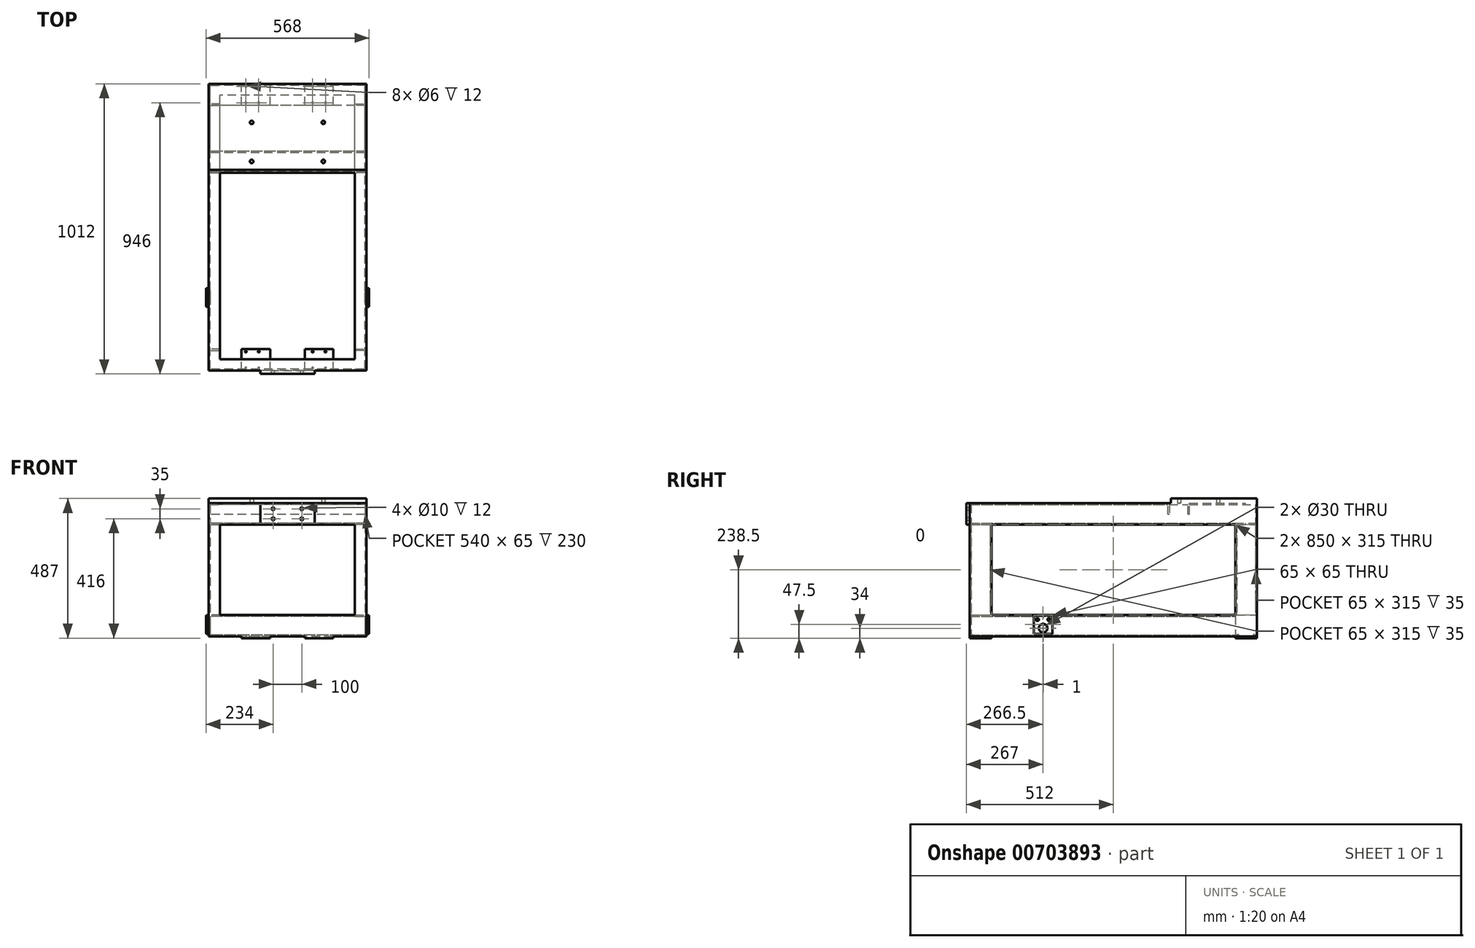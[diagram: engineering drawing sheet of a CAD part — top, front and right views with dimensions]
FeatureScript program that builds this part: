
annotation { "Feature Type Name" : "Feature", "Feature Type Description" : "" }
export const myFeature = defineFeature(function(context is Context, id is Id, definition is map)
    precondition{}
    {
        {
            var Q0;
            Q0=qCreatedBy(makeId("Front.planeOp"),FACE);
            var sketch = newSketch(context, id + "F0", { "sketchPlane" : qUnion([Q0])});
            skLineSegment(sketch, "E0", {"start": v(0, 32.91) * mm, "end": v(0, -75) * mm});
            skLineSegment(sketch, "E1", {"start": v(0, -75) * mm, "end": v(40, -75) * mm});
            skLineSegment(sketch, "E2", {"start": v(40, -75) * mm, "end": v(40, -70) * mm});
            skLineSegment(sketch, "E3", {"start": v(40, -70) * mm, "end": v(5, -70) * mm});
            skLineSegment(sketch, "E4", {"start": v(5, -70) * mm, "end": v(5, -5) * mm});
            skLineSegment(sketch, "E5", {"start": v(5, -5) * mm, "end": v(40, -5) * mm});
            skLineSegment(sketch, "E6", {"start": v(40, -5) * mm, "end": v(40, 0) * mm});
            skLineSegment(sketch, "E7", {"start": v(40, 0) * mm, "end": v(0, 0) * mm});
            skLineSegment(sketch, "E8.MirrorCS", {"start": v(510, -70) * mm, "end": v(545, -70) * mm});
            skLineSegment(sketch, "E9.MirrorCS", {"start": v(545, -70) * mm, "end": v(545, -5) * mm});
            skLineSegment(sketch, "E10.MirrorCS", {"start": v(545, -5) * mm, "end": v(510, -5) * mm});
            skLineSegment(sketch, "E11.MirrorCS", {"start": v(510, -5) * mm, "end": v(510, 0) * mm});
            skLineSegment(sketch, "E12.MirrorCS", {"start": v(510, 0) * mm, "end": v(550, 0) * mm});
            skLineSegment(sketch, "E13.MirrorCS", {"start": v(510, -75) * mm, "end": v(510, -70) * mm});
            skLineSegment(sketch, "E14.MirrorCS", {"start": v(550, 0) * mm, "end": v(550, -75) * mm});
            skLineSegment(sketch, "E15.MirrorCS", {"start": v(550, -75) * mm, "end": v(510, -75) * mm});
            skLineSegment(sketch, "E16", {"start": v(0, -357.09) * mm, "end": v(0, -465) * mm});
            skLineSegment(sketch, "E17", {"start": v(0, -465) * mm, "end": v(40, -465) * mm});
            skLineSegment(sketch, "E18", {"start": v(40, -465) * mm, "end": v(40, -460) * mm});
            skLineSegment(sketch, "E19", {"start": v(40, -460) * mm, "end": v(5, -460) * mm});
            skLineSegment(sketch, "E20", {"start": v(5, -460) * mm, "end": v(5, -395) * mm});
            skLineSegment(sketch, "E21", {"start": v(5, -395) * mm, "end": v(40, -395) * mm});
            skLineSegment(sketch, "E22", {"start": v(40, -395) * mm, "end": v(40, -390) * mm});
            skLineSegment(sketch, "E23", {"start": v(40, -390) * mm, "end": v(0, -390) * mm});
            skLineSegment(sketch, "E24.MirrorCS", {"start": v(510, -460) * mm, "end": v(545, -460) * mm});
            skLineSegment(sketch, "E25.MirrorCS", {"start": v(545, -460) * mm, "end": v(545, -395) * mm});
            skLineSegment(sketch, "E26.MirrorCS", {"start": v(545, -395) * mm, "end": v(510, -395) * mm});
            skLineSegment(sketch, "E27.MirrorCS", {"start": v(510, -395) * mm, "end": v(510, -390) * mm});
            skLineSegment(sketch, "E28.MirrorCS", {"start": v(510, -390) * mm, "end": v(550, -390) * mm});
            skLineSegment(sketch, "E29.MirrorCS", {"start": v(510, -465) * mm, "end": v(510, -460) * mm});
            skLineSegment(sketch, "E30.MirrorCS", {"start": v(550, -390) * mm, "end": v(550, -465) * mm});
            skLineSegment(sketch, "E31.MirrorCS", {"start": v(550, -465) * mm, "end": v(510, -465) * mm});
            skSolve(sketch);
        }
        {
            var Q0;
            {var subQ0=sQuery(id+"F0.wireOp",EDGE,"E1");Q0=makeQuery(id+"F0.imprint","IMPRINT",FACE,{"disambiguationData":[TD([[makeQuery(id+"F0.imprint","IMPRINT",EDGE,{"derivedFrom":subQ0}),1.0]])]});}
            var Q1;
            Q1=makeQuery(id+"F0.imprint","IMPRINT",FACE,{"disambiguationData":[TD([[makeQuery(id+"F0.imprint","IMPRINT",EDGE,{"derivedFrom":sQuery(id+"F0.wireOp",EDGE,"E8.MirrorCS")}),-1.0]])]});
            var Q2;
            {var subQ0=sQuery(id+"F0.wireOp",EDGE,"E17");Q2=makeQuery(id+"F0.imprint","IMPRINT",FACE,{"disambiguationData":[TD([[makeQuery(id+"F0.imprint","IMPRINT",EDGE,{"derivedFrom":subQ0}),1.0]])]});}
            var Q3;
            Q3=makeQuery(id+"F0.imprint","IMPRINT",FACE,{"disambiguationData":[TD([[makeQuery(id+"F0.imprint","IMPRINT",EDGE,{"derivedFrom":sQuery(id+"F0.wireOp",EDGE,"E24.MirrorCS")}),-1.0]])]});
            extrude(context, id + "F1", {"entities" : qUnion([Q0, Q1, Q2, Q3]), "depth" : 1000 * mm, "offsetDistance" : 25 * mm});
        }
        {
            var Q0;
            Q0=qCreatedBy(makeId("Right.planeOp"),FACE);
            var sketch = newSketch(context, id + "F2", { "sketchPlane" : qUnion([Q0])});
            skLineSegment(sketch, "E32", {"start": v(0, -75) * mm, "end": v(0, 0) * mm});
            skLineSegment(sketch, "E33", {"start": v(-40, 0) * mm, "end": v(-40, -5) * mm});
            skLineSegment(sketch, "E34", {"start": v(-40, -5) * mm, "end": v(-5, -5) * mm});
            skLineSegment(sketch, "E35", {"start": v(-5, -5) * mm, "end": v(-5, -70) * mm});
            skLineSegment(sketch, "E36", {"start": v(-5, -70) * mm, "end": v(-40, -70) * mm});
            skLineSegment(sketch, "E37", {"start": v(-40, -70) * mm, "end": v(-40, -75) * mm});
            skLineSegment(sketch, "E38", {"start": v(-40, -75) * mm, "end": v(0, -75) * mm});
            skLineSegment(sketch, "E39", {"start": v(-40, 0) * mm, "end": v(0, 0) * mm});
            skLineSegment(sketch, "E40.MirrorCS", {"start": v(-960, 0) * mm, "end": v(-960, -5) * mm});
            skLineSegment(sketch, "E41.MirrorCS", {"start": v(-960, -70) * mm, "end": v(-960, -75) * mm});
            skLineSegment(sketch, "E42.MirrorCS", {"start": v(-960, -5) * mm, "end": v(-995, -5) * mm});
            skLineSegment(sketch, "E43.MirrorCS", {"start": v(-995, -5) * mm, "end": v(-995, -70) * mm});
            skLineSegment(sketch, "E44.MirrorCS", {"start": v(-995, -70) * mm, "end": v(-960, -70) * mm});
            skLineSegment(sketch, "E45.MirrorCS", {"start": v(-960, 0) * mm, "end": v(-1000, 0) * mm});
            skLineSegment(sketch, "E46.MirrorCS", {"start": v(-1000, -75) * mm, "end": v(-1000, 0) * mm});
            skLineSegment(sketch, "E47.MirrorCS", {"start": v(-960, -75) * mm, "end": v(-1000, -75) * mm});
            skLineSegment(sketch, "E48.MirrorCS", {"start": v(-235, -40) * mm, "end": v(-240, -40) * mm});
            skLineSegment(sketch, "E49.MirrorCS", {"start": v(-305, -40) * mm, "end": v(-310, -40) * mm});
            skLineSegment(sketch, "E50.MirrorCS", {"start": v(-240, -40) * mm, "end": v(-240, -5) * mm});
            skLineSegment(sketch, "E51.MirrorCS", {"start": v(-240, -5) * mm, "end": v(-305, -5) * mm});
            skLineSegment(sketch, "E52.MirrorCS", {"start": v(-305, -5) * mm, "end": v(-305, -40) * mm});
            skLineSegment(sketch, "E53.MirrorCS", {"start": v(-235, -40) * mm, "end": v(-235, 0) * mm});
            skLineSegment(sketch, "E54.MirrorCS", {"start": v(-310, 0) * mm, "end": v(-235, 0) * mm});
            skLineSegment(sketch, "E55.MirrorCS", {"start": v(-310, -40) * mm, "end": v(-310, 0) * mm});
            skLineSegment(sketch, "E56.MirrorCS", {"start": v(-960, -390) * mm, "end": v(-960, -395) * mm});
            skLineSegment(sketch, "E57.MirrorCS", {"start": v(-960, -460) * mm, "end": v(-960, -465) * mm});
            skLineSegment(sketch, "E58.MirrorCS", {"start": v(-960, -395) * mm, "end": v(-995, -395) * mm});
            skLineSegment(sketch, "E59.MirrorCS", {"start": v(-995, -395) * mm, "end": v(-995, -460) * mm});
            skLineSegment(sketch, "E60.MirrorCS", {"start": v(-995, -460) * mm, "end": v(-960, -460) * mm});
            skLineSegment(sketch, "E61.MirrorCS", {"start": v(-960, -390) * mm, "end": v(-1000, -390) * mm});
            skLineSegment(sketch, "E62.MirrorCS", {"start": v(0, -465) * mm, "end": v(0, -390) * mm});
            skLineSegment(sketch, "E63.MirrorCS", {"start": v(-960, -465) * mm, "end": v(-1000, -465) * mm});
            skLineSegment(sketch, "E64", {"start": v(-1000, -465) * mm, "end": v(-1000, -390) * mm});
            skLineSegment(sketch, "E65.bottom", {"start": v(0, -390) * mm, "end": v(-75, -390) * mm});
            skLineSegment(sketch, "E65.top", {"start": v(0, -465) * mm, "end": v(-75, -465) * mm});
            skLineSegment(sketch, "E65.left", {"start": v(0, -390) * mm, "end": v(0, -465) * mm});
            skLineSegment(sketch, "E65.right", {"start": v(-75, -390) * mm, "end": v(-75, -465) * mm});
            skSolve(sketch);
        }
        {
            var Q0;
            Q0=qSketchRegion(id+"F2",true);
            extrude(context, id + "F3", {"entities" : qUnion([Q0]), "depth" : 550 * mm, "offsetDistance" : 25 * mm});
        }
        {
            var Q0;
            Q0=makeQuery(id+"F3.opExtrude","SWEPT_FACE",FACE,{"disambiguationData":[OSD([sQuery(id+"F2.wireOp",EDGE,"E65.bottom")])]});
            var sketch = newSketch(context, id + "F4", { "sketchPlane" : qUnion([Q0])});
            skLineSegment(sketch, "E66", {"start": v(0, -1000) * mm, "end": v(40, -1000) * mm});
            skLineSegment(sketch, "E67", {"start": v(40, -1000) * mm, "end": v(40, -995) * mm});
            skLineSegment(sketch, "E68", {"start": v(40, -995) * mm, "end": v(5, -995) * mm});
            skLineSegment(sketch, "E69", {"start": v(5, -995) * mm, "end": v(5, -930) * mm});
            skLineSegment(sketch, "E70", {"start": v(5, -930) * mm, "end": v(40, -930) * mm});
            skLineSegment(sketch, "E71", {"start": v(40, -930) * mm, "end": v(40, -925) * mm});
            skLineSegment(sketch, "E72", {"start": v(40, -925) * mm, "end": v(0, -925) * mm});
            skLineSegment(sketch, "E73.MirrorCS", {"start": v(510, -995) * mm, "end": v(545, -995) * mm});
            skLineSegment(sketch, "E74.MirrorCS", {"start": v(545, -995) * mm, "end": v(545, -930) * mm});
            skLineSegment(sketch, "E75.MirrorCS", {"start": v(545, -930) * mm, "end": v(510, -930) * mm});
            skLineSegment(sketch, "E76.MirrorCS", {"start": v(510, -930) * mm, "end": v(510, -925) * mm});
            skLineSegment(sketch, "E77.MirrorCS", {"start": v(510, -925) * mm, "end": v(550, -925) * mm});
            skLineSegment(sketch, "E78.MirrorCS", {"start": v(510, -1000) * mm, "end": v(510, -995) * mm});
            skLineSegment(sketch, "E79.MirrorCS", {"start": v(550, -925) * mm, "end": v(550, -1000) * mm});
            skLineSegment(sketch, "E80.MirrorCS", {"start": v(550, -1000) * mm, "end": v(510, -1000) * mm});
            skLineSegment(sketch, "E81", {"start": v(0, -1000) * mm, "end": v(0, -925) * mm});
            skLineSegment(sketch, "E82", {"start": v(0, -75) * mm, "end": v(40, -75) * mm});
            skLineSegment(sketch, "E83", {"start": v(40, -75) * mm, "end": v(40, -70) * mm});
            skLineSegment(sketch, "E84", {"start": v(40, -70) * mm, "end": v(5, -70) * mm});
            skLineSegment(sketch, "E85", {"start": v(5, -70) * mm, "end": v(5, -5) * mm});
            skLineSegment(sketch, "E86", {"start": v(5, -5) * mm, "end": v(40, -5) * mm});
            skLineSegment(sketch, "E87", {"start": v(40, -5) * mm, "end": v(40, 0) * mm});
            skLineSegment(sketch, "E88", {"start": v(40, 0) * mm, "end": v(0, 0) * mm});
            skLineSegment(sketch, "E89.MirrorCS", {"start": v(510, -70) * mm, "end": v(545, -70) * mm});
            skLineSegment(sketch, "E90.MirrorCS", {"start": v(545, -70) * mm, "end": v(545, -5) * mm});
            skLineSegment(sketch, "E91.MirrorCS", {"start": v(545, -5) * mm, "end": v(510, -5) * mm});
            skLineSegment(sketch, "E92.MirrorCS", {"start": v(510, -5) * mm, "end": v(510, 0) * mm});
            skLineSegment(sketch, "E93.MirrorCS", {"start": v(510, 0) * mm, "end": v(550, 0) * mm});
            skLineSegment(sketch, "E94.MirrorCS", {"start": v(510, -75) * mm, "end": v(510, -70) * mm});
            skLineSegment(sketch, "E95.MirrorCS", {"start": v(550, 0) * mm, "end": v(550, -75) * mm});
            skLineSegment(sketch, "E96.MirrorCS", {"start": v(550, -75) * mm, "end": v(510, -75) * mm});
            skLineSegment(sketch, "E97", {"start": v(0, -75) * mm, "end": v(0, 0) * mm});
            skSolve(sketch);
        }
        {
            var Q0;
            Q0 = qSketchRegion(id + "F4", true);
            extrude(context, id + "F5", {"entities" : qUnion([Q0]), "depth" : 315 * mm, "offsetDistance" : 25 * mm});
        }
        {
            var Q0;
            Q0=qCreatedBy(makeId("Top.planeOp"),FACE);
            var sketch = newSketch(context, id + "F6", { "sketchPlane" : qUnion([Q0])});
            skLineSegment(sketch, "E98.bottom", {"start": v(0, 0) * mm, "end": v(550, 0) * mm});
            skLineSegment(sketch, "E98.top", {"start": v(0, -300) * mm, "end": v(550, -300) * mm});
            skLineSegment(sketch, "E98.left", {"start": v(0, 0) * mm, "end": v(0, -300) * mm});
            skLineSegment(sketch, "E98.right", {"start": v(550, 0) * mm, "end": v(550, -300) * mm});
            skCircle(sketch, "E99", {"center": v(150, -134.83) * mm, "radius": 6 * mm});
            skCircle(sketch, "E100", {"center": v(400, -134.83) * mm, "radius": 6 * mm});
            skCircle(sketch, "E101", {"center": v(150, -270.83) * mm, "radius": 6 * mm});
            skCircle(sketch, "E102", {"center": v(400, -270.83) * mm, "radius": 6 * mm});
            skSolve(sketch);
        }
        {
            var Q0;
            Q0 = qSketchRegion(id + "F6", true);
            extrude(context, id + "F7", {"entities" : qUnion([Q0]), "depth" : 16 * mm, "offsetDistance" : 25 * mm});
        }
        {
            var Q0;
            Q0=makeQuery(id+"F3.opExtrude","SWEPT_FACE",FACE,{"disambiguationData":[OSD([sQuery(id+"F2.wireOp",EDGE,"E46.MirrorCS")])]});
            cPlane(context, id + "F8", {"entities" : qUnion([Q0]), "cplaneType" : CPlaneType.OFFSET, "offset" : 0 * mm, "width" : 150 * mm, "height" : 150 * mm});
        }
        {
            var Q0;
            Q0=qCreatedBy(id+"F8.planeOp",FACE);
            var sketch = newSketch(context, id + "F9", { "sketchPlane" : qUnion([Q0])});
            skLineSegment(sketch, "E103.bottom", {"start": v(370, 0) * mm, "end": v(180, 0) * mm});
            skLineSegment(sketch, "E103.top", {"start": v(370, -75) * mm, "end": v(180, -75) * mm});
            skLineSegment(sketch, "E103.left", {"start": v(370, 0) * mm, "end": v(370, -75) * mm});
            skLineSegment(sketch, "E103.right", {"start": v(180, 0) * mm, "end": v(180, -75) * mm});
            skCircle(sketch, "E104", {"center": v(225, -20) * mm, "radius": 5 * mm});
            skCircle(sketch, "E105", {"center": v(225, -55) * mm, "radius": 5 * mm});
            skCircle(sketch, "E106", {"center": v(325, -20) * mm, "radius": 5 * mm});
            skCircle(sketch, "E107", {"center": v(325, -55) * mm, "radius": 5 * mm});
            skSolve(sketch);
        }
        {
            var Q0;
            Q0 = qSketchRegion(id + "F9", true);
            extrude(context, id + "F10", {"entities" : qUnion([Q0]), "operationType" : NewBodyOperationType.ADD, "depth" : 12 * mm, "offsetDistance" : 25 * mm});
        }
        {
            var Q0;
            Q0=makeQuery(id+"F1.opExtrude","SWEPT_FACE",FACE,{"disambiguationData":[OSD([sQuery(id+"F0.wireOp",EDGE,"E31.MirrorCS")])]});
            cPlane(context, id + "F11", {"entities" : qUnion([Q0]), "cplaneType" : CPlaneType.OFFSET, "offset" : 0 * mm, "width" : 150 * mm, "height" : 150 * mm});
        }
        {
            var Q0;
            Q0=qCreatedBy(id+"F11.planeOp",FACE);
            var sketch = newSketch(context, id + "F12", { "sketchPlane" : qUnion([Q0])});
            skLineSegment(sketch, "E108.bottom", {"start": v(215, 75) * mm, "end": v(115, 75) * mm});
            skLineSegment(sketch, "E108.top", {"start": v(215, 0) * mm, "end": v(115, 0) * mm});
            skLineSegment(sketch, "E108.left", {"start": v(215, 75) * mm, "end": v(215, 0) * mm});
            skLineSegment(sketch, "E108.right", {"start": v(115, 75) * mm, "end": v(115, 0) * mm});
            skLineSegment(sketch, "E109.bottom", {"start": v(435, 75) * mm, "end": v(335, 75) * mm});
            skLineSegment(sketch, "E109.top", {"start": v(435, 0) * mm, "end": v(335, 0) * mm});
            skLineSegment(sketch, "E109.left", {"start": v(435, 75) * mm, "end": v(435, 0) * mm});
            skLineSegment(sketch, "E109.right", {"start": v(335, 75) * mm, "end": v(335, 0) * mm});
            skLineSegment(sketch, "E110.bottom", {"start": v(215, 1000) * mm, "end": v(115, 1000) * mm});
            skLineSegment(sketch, "E110.top", {"start": v(215, 925) * mm, "end": v(115, 925) * mm});
            skLineSegment(sketch, "E110.left", {"start": v(215, 1000) * mm, "end": v(215, 925) * mm});
            skLineSegment(sketch, "E110.right", {"start": v(115, 1000) * mm, "end": v(115, 925) * mm});
            skLineSegment(sketch, "E111.bottom", {"start": v(435, 1000) * mm, "end": v(335, 1000) * mm});
            skLineSegment(sketch, "E111.top", {"start": v(435, 925) * mm, "end": v(335, 925) * mm});
            skLineSegment(sketch, "E111.left", {"start": v(435, 1000) * mm, "end": v(435, 925) * mm});
            skLineSegment(sketch, "E111.right", {"start": v(335, 1000) * mm, "end": v(335, 925) * mm});
            skSolve(sketch);
        }
        {
            var Q0;
            Q0=makeQuery(id+"F1.opExtrude","SWEPT_BODY",BODY,{"disambiguationData":[OSD([sQuery(id+"F0.wireOp",EDGE,"E0"),sQuery(id+"F0.wireOp",EDGE,"E1"),sQuery(id+"F0.wireOp",EDGE,"E2"),sQuery(id+"F0.wireOp",EDGE,"E3"),sQuery(id+"F0.wireOp",EDGE,"E4"),sQuery(id+"F0.wireOp",EDGE,"E5"),sQuery(id+"F0.wireOp",EDGE,"E6"),sQuery(id+"F0.wireOp",EDGE,"E7")])]});
            var Q1;
            Q1=makeQuery(id+"F1.opExtrude","SWEPT_BODY",BODY,{"disambiguationData":[OSD([sQuery(id+"F0.wireOp",EDGE,"E8.MirrorCS"),sQuery(id+"F0.wireOp",EDGE,"E9.MirrorCS"),sQuery(id+"F0.wireOp",EDGE,"E10.MirrorCS"),sQuery(id+"F0.wireOp",EDGE,"E11.MirrorCS"),sQuery(id+"F0.wireOp",EDGE,"E12.MirrorCS"),sQuery(id+"F0.wireOp",EDGE,"E13.MirrorCS"),sQuery(id+"F0.wireOp",EDGE,"E14.MirrorCS"),sQuery(id+"F0.wireOp",EDGE,"E15.MirrorCS")])]});
            var Q2;
            Q2=makeQuery(id+"F1.opExtrude","SWEPT_BODY",BODY,{"disambiguationData":[OSD([sQuery(id+"F0.wireOp",EDGE,"E16"),sQuery(id+"F0.wireOp",EDGE,"E17"),sQuery(id+"F0.wireOp",EDGE,"E18"),sQuery(id+"F0.wireOp",EDGE,"E19"),sQuery(id+"F0.wireOp",EDGE,"E20"),sQuery(id+"F0.wireOp",EDGE,"E21"),sQuery(id+"F0.wireOp",EDGE,"E22"),sQuery(id+"F0.wireOp",EDGE,"E23")])]});
            var Q3;
            Q3=makeQuery(id+"F1.opExtrude","SWEPT_BODY",BODY,{"disambiguationData":[OSD([sQuery(id+"F0.wireOp",EDGE,"E24.MirrorCS"),sQuery(id+"F0.wireOp",EDGE,"E25.MirrorCS"),sQuery(id+"F0.wireOp",EDGE,"E26.MirrorCS"),sQuery(id+"F0.wireOp",EDGE,"E27.MirrorCS"),sQuery(id+"F0.wireOp",EDGE,"E28.MirrorCS"),sQuery(id+"F0.wireOp",EDGE,"E29.MirrorCS"),sQuery(id+"F0.wireOp",EDGE,"E30.MirrorCS"),sQuery(id+"F0.wireOp",EDGE,"E31.MirrorCS")])]});
            var Q4;
            Q4=makeQuery(id+"F3.opExtrude","SWEPT_BODY",BODY,{"disambiguationData":[OSD([sQuery(id+"F2.wireOp",EDGE,"E32"),sQuery(id+"F2.wireOp",EDGE,"E33"),sQuery(id+"F2.wireOp",EDGE,"E34"),sQuery(id+"F2.wireOp",EDGE,"E35"),sQuery(id+"F2.wireOp",EDGE,"E36"),sQuery(id+"F2.wireOp",EDGE,"E37"),sQuery(id+"F2.wireOp",EDGE,"E38"),sQuery(id+"F2.wireOp",EDGE,"E39")])]});
            var Q5;
            Q5=makeQuery(id+"F3.opExtrude","SWEPT_BODY",BODY,{"disambiguationData":[OSD([sQuery(id+"F2.wireOp",EDGE,"E56.MirrorCS"),sQuery(id+"F2.wireOp",EDGE,"E57.MirrorCS"),sQuery(id+"F2.wireOp",EDGE,"E58.MirrorCS"),sQuery(id+"F2.wireOp",EDGE,"E59.MirrorCS"),sQuery(id+"F2.wireOp",EDGE,"E60.MirrorCS"),sQuery(id+"F2.wireOp",EDGE,"E61.MirrorCS"),sQuery(id+"F2.wireOp",EDGE,"E63.MirrorCS"),sQuery(id+"F2.wireOp",EDGE,"E64")])]});
            var Q6;
            Q6=makeQuery(id+"F5.opExtrude","SWEPT_BODY",BODY,{"disambiguationData":[OSD([sQuery(id+"F4.wireOp",EDGE,"E73.MirrorCS"),sQuery(id+"F4.wireOp",EDGE,"E74.MirrorCS"),sQuery(id+"F4.wireOp",EDGE,"E75.MirrorCS"),sQuery(id+"F4.wireOp",EDGE,"E76.MirrorCS"),sQuery(id+"F4.wireOp",EDGE,"E77.MirrorCS"),sQuery(id+"F4.wireOp",EDGE,"E78.MirrorCS"),sQuery(id+"F4.wireOp",EDGE,"E79.MirrorCS"),sQuery(id+"F4.wireOp",EDGE,"E80.MirrorCS")])]});
            var Q7;
            Q7=makeQuery(id+"F7.opExtrude","SWEPT_BODY",BODY,{"disambiguationData":[OSD([sQuery(id+"F6.wireOp",EDGE,"E98.bottom"),sQuery(id+"F6.wireOp",EDGE,"E98.top"),sQuery(id+"F6.wireOp",EDGE,"E98.left"),sQuery(id+"F6.wireOp",EDGE,"E98.right"),sQuery(id+"F6.wireOp",EDGE,"E99"),sQuery(id+"F6.wireOp",EDGE,"E100"),sQuery(id+"F6.wireOp",EDGE,"E101"),sQuery(id+"F6.wireOp",EDGE,"E102")])]});
            var Q8;
            Q8=makeQuery(id+"F3.opExtrude","SWEPT_BODY",BODY,{"disambiguationData":[OSD([sQuery(id+"F2.wireOp",EDGE,"E40.MirrorCS"),sQuery(id+"F2.wireOp",EDGE,"E41.MirrorCS"),sQuery(id+"F2.wireOp",EDGE,"E42.MirrorCS"),sQuery(id+"F2.wireOp",EDGE,"E43.MirrorCS"),sQuery(id+"F2.wireOp",EDGE,"E44.MirrorCS"),sQuery(id+"F2.wireOp",EDGE,"E45.MirrorCS"),sQuery(id+"F2.wireOp",EDGE,"E46.MirrorCS"),sQuery(id+"F2.wireOp",EDGE,"E47.MirrorCS")])]});
            var Q9;
            Q9=makeQuery(id+"F3.opExtrude","SWEPT_BODY",BODY,{"disambiguationData":[OSD([sQuery(id+"F2.wireOp",EDGE,"E48.MirrorCS"),sQuery(id+"F2.wireOp",EDGE,"E49.MirrorCS"),sQuery(id+"F2.wireOp",EDGE,"E50.MirrorCS"),sQuery(id+"F2.wireOp",EDGE,"E51.MirrorCS"),sQuery(id+"F2.wireOp",EDGE,"E52.MirrorCS"),sQuery(id+"F2.wireOp",EDGE,"E53.MirrorCS"),sQuery(id+"F2.wireOp",EDGE,"E54.MirrorCS"),sQuery(id+"F2.wireOp",EDGE,"E55.MirrorCS")])]});
            var Q10;
            Q10=makeQuery(id+"F3.opExtrude","SWEPT_BODY",BODY,{"disambiguationData":[OSD([sQuery(id+"F2.wireOp",EDGE,"E65.bottom"),sQuery(id+"F2.wireOp",EDGE,"E65.top"),sQuery(id+"F2.wireOp",EDGE,"E65.left"),sQuery(id+"F2.wireOp",EDGE,"E65.right")])]});
            var Q11;
            Q11=makeQuery(id+"F5.opExtrude","SWEPT_BODY",BODY,{"disambiguationData":[OSD([sQuery(id+"F4.wireOp",EDGE,"E66"),sQuery(id+"F4.wireOp",EDGE,"E67"),sQuery(id+"F4.wireOp",EDGE,"E68"),sQuery(id+"F4.wireOp",EDGE,"E69"),sQuery(id+"F4.wireOp",EDGE,"E70"),sQuery(id+"F4.wireOp",EDGE,"E71"),sQuery(id+"F4.wireOp",EDGE,"E72"),sQuery(id+"F4.wireOp",EDGE,"E81")])]});
            var Q12;
            Q12=makeQuery(id+"F5.opExtrude","SWEPT_BODY",BODY,{"disambiguationData":[OSD([sQuery(id+"F4.wireOp",EDGE,"E82"),sQuery(id+"F4.wireOp",EDGE,"E83"),sQuery(id+"F4.wireOp",EDGE,"E84"),sQuery(id+"F4.wireOp",EDGE,"E85"),sQuery(id+"F4.wireOp",EDGE,"E86"),sQuery(id+"F4.wireOp",EDGE,"E87"),sQuery(id+"F4.wireOp",EDGE,"E88"),sQuery(id+"F4.wireOp",EDGE,"E97")])]});
            var Q13;
            Q13=makeQuery(id+"F5.opExtrude","SWEPT_BODY",BODY,{"disambiguationData":[OSD([sQuery(id+"F4.wireOp",EDGE,"E89.MirrorCS"),sQuery(id+"F4.wireOp",EDGE,"E90.MirrorCS"),sQuery(id+"F4.wireOp",EDGE,"E91.MirrorCS"),sQuery(id+"F4.wireOp",EDGE,"E92.MirrorCS"),sQuery(id+"F4.wireOp",EDGE,"E93.MirrorCS"),sQuery(id+"F4.wireOp",EDGE,"E94.MirrorCS"),sQuery(id+"F4.wireOp",EDGE,"E95.MirrorCS"),sQuery(id+"F4.wireOp",EDGE,"E96.MirrorCS")])]});
            booleanBodies(context, id + "F13", {"operationType" : BooleanOperationType.UNION, "tools" : qUnion([Q0, Q1, Q2, Q3, Q4, Q5, Q6, Q7, Q8, Q9, Q10, Q11, Q12, Q13])});
        }
        {
            var Q0;
            Q0 = qSketchRegion(id + "F12", true);
            extrude(context, id + "F14", {"entities" : qUnion([Q0]), "operationType" : NewBodyOperationType.ADD, "depth" : 6 * mm, "offsetDistance" : 25 * mm});
        }
        {
            var Q0;
            Q0=makeQuery(id+"F14.opExtrude","CAP_FACE",FACE,{"disambiguationData":[OSD([sQuery(id+"F12.wireOp",EDGE,"E111.bottom"),sQuery(id+"F12.wireOp",EDGE,"E111.top"),sQuery(id+"F12.wireOp",EDGE,"E111.left"),sQuery(id+"F12.wireOp",EDGE,"E111.right")])],"isStart":false});
            cPlane(context, id + "F15", {"entities" : qUnion([Q0]), "cplaneType" : CPlaneType.OFFSET, "offset" : 0 * mm, "width" : 150 * mm, "height" : 150 * mm});
        }
        {
            var Q0;
            Q0=qCreatedBy(id+"F15.planeOp",FACE);
            var sketch = newSketch(context, id + "F16", { "sketchPlane" : qUnion([Q0])});
            skCircle(sketch, "E112", {"center": v(407.5, 934) * mm, "radius": 3 * mm});
            skCircle(sketch, "E113", {"center": v(407.5, 991) * mm, "radius": 3 * mm});
            skCircle(sketch, "E114", {"center": v(362.5, 991) * mm, "radius": 3 * mm});
            skCircle(sketch, "E115", {"center": v(362.5, 934) * mm, "radius": 3 * mm});
            skCircle(sketch, "E116", {"center": v(407.5, 9) * mm, "radius": 3 * mm});
            skCircle(sketch, "E117", {"center": v(407.5, 66) * mm, "radius": 3 * mm});
            skCircle(sketch, "E118", {"center": v(362.5, 66) * mm, "radius": 3 * mm});
            skCircle(sketch, "E119", {"center": v(362.5, 9) * mm, "radius": 3 * mm});
            skCircle(sketch, "E120", {"center": v(174.84, 934) * mm, "radius": 3 * mm});
            skCircle(sketch, "E121", {"center": v(174.84, 991) * mm, "radius": 3 * mm});
            skCircle(sketch, "E122", {"center": v(129.84, 991) * mm, "radius": 3 * mm});
            skCircle(sketch, "E123", {"center": v(129.84, 934) * mm, "radius": 3 * mm});
            skCircle(sketch, "E124", {"center": v(174.84, 9) * mm, "radius": 3 * mm});
            skCircle(sketch, "E125", {"center": v(174.84, 66) * mm, "radius": 3 * mm});
            skCircle(sketch, "E126", {"center": v(129.84, 66) * mm, "radius": 3 * mm});
            skCircle(sketch, "E127", {"center": v(129.84, 9) * mm, "radius": 3 * mm});
            skSolve(sketch);
        }
        {
            var Q0;
            Q0 = qSketchRegion(id + "F16", true);
            extrude(context, id + "F17", {"entities" : qUnion([Q0]), "operationType" : NewBodyOperationType.REMOVE, "oppositeDirection" : true, "depth" : 12 * mm, "offsetDistance" : 25 * mm});
        }
        {
            var Q0;
            Q0=qCreatedBy(makeId("Right.planeOp"),FACE);
            var sketch = newSketch(context, id + "F18", { "sketchPlane" : qUnion([Q0])});
            skLineSegment(sketch, "E128.bottom", {"start": v(-712.5, -391) * mm, "end": v(-777.5, -391) * mm});
            skLineSegment(sketch, "E128.top", {"start": v(-712.5, -456) * mm, "end": v(-777.5, -456) * mm});
            skLineSegment(sketch, "E128.left", {"start": v(-712.5, -391) * mm, "end": v(-712.5, -456) * mm});
            skLineSegment(sketch, "E128.right", {"start": v(-777.5, -391) * mm, "end": v(-777.5, -456) * mm});
            skSolve(sketch);
        }
        {
            var Q0;
            Q0 = qSketchRegion(id + "F18", true);
            extrude(context, id + "F19", {"entities" : qUnion([Q0]), "operationType" : NewBodyOperationType.ADD, "oppositeDirection" : true, "depth" : 9 * mm, "offsetDistance" : 25 * mm});
        }
        {
            var Q0;
            Q0=makeQuery(id+"F13.opBoolean","MERGE",FACE,{"derivedFrom":[makeQuery(id+"F1.opExtrude","SWEPT_FACE",FACE,{"disambiguationData":[OSD([sQuery(id+"F0.wireOp",EDGE,"E14.MirrorCS")])]}),makeQuery(id+"F1.opExtrude","SWEPT_FACE",FACE,{"disambiguationData":[OSD([sQuery(id+"F0.wireOp",EDGE,"E30.MirrorCS")])]}),makeQuery(id+"F3.opExtrude","CAP_FACE",FACE,{"disambiguationData":[OSD([sQuery(id+"F2.wireOp",EDGE,"E32"),sQuery(id+"F2.wireOp",EDGE,"E33"),sQuery(id+"F2.wireOp",EDGE,"E34"),sQuery(id+"F2.wireOp",EDGE,"E35"),sQuery(id+"F2.wireOp",EDGE,"E36"),sQuery(id+"F2.wireOp",EDGE,"E37"),sQuery(id+"F2.wireOp",EDGE,"E38"),sQuery(id+"F2.wireOp",EDGE,"E39")])],"isStart":false}),makeQuery(id+"F3.opExtrude","CAP_FACE",FACE,{"disambiguationData":[OSD([sQuery(id+"F2.wireOp",EDGE,"E40.MirrorCS"),sQuery(id+"F2.wireOp",EDGE,"E41.MirrorCS"),sQuery(id+"F2.wireOp",EDGE,"E42.MirrorCS"),sQuery(id+"F2.wireOp",EDGE,"E43.MirrorCS"),sQuery(id+"F2.wireOp",EDGE,"E44.MirrorCS"),sQuery(id+"F2.wireOp",EDGE,"E45.MirrorCS"),sQuery(id+"F2.wireOp",EDGE,"E46.MirrorCS"),sQuery(id+"F2.wireOp",EDGE,"E47.MirrorCS")])],"isStart":false}),makeQuery(id+"F3.opExtrude","CAP_FACE",FACE,{"disambiguationData":[OSD([sQuery(id+"F2.wireOp",EDGE,"E48.MirrorCS"),sQuery(id+"F2.wireOp",EDGE,"E49.MirrorCS"),sQuery(id+"F2.wireOp",EDGE,"E50.MirrorCS"),sQuery(id+"F2.wireOp",EDGE,"E51.MirrorCS"),sQuery(id+"F2.wireOp",EDGE,"E52.MirrorCS"),sQuery(id+"F2.wireOp",EDGE,"E53.MirrorCS"),sQuery(id+"F2.wireOp",EDGE,"E54.MirrorCS"),sQuery(id+"F2.wireOp",EDGE,"E55.MirrorCS")])],"isStart":false}),makeQuery(id+"F3.opExtrude","CAP_FACE",FACE,{"disambiguationData":[OSD([sQuery(id+"F2.wireOp",EDGE,"E56.MirrorCS"),sQuery(id+"F2.wireOp",EDGE,"E57.MirrorCS"),sQuery(id+"F2.wireOp",EDGE,"E58.MirrorCS"),sQuery(id+"F2.wireOp",EDGE,"E59.MirrorCS"),sQuery(id+"F2.wireOp",EDGE,"E60.MirrorCS"),sQuery(id+"F2.wireOp",EDGE,"E61.MirrorCS"),sQuery(id+"F2.wireOp",EDGE,"E63.MirrorCS"),sQuery(id+"F2.wireOp",EDGE,"E64")])],"isStart":false}),makeQuery(id+"F3.opExtrude","CAP_FACE",FACE,{"disambiguationData":[OSD([sQuery(id+"F2.wireOp",EDGE,"E65.bottom"),sQuery(id+"F2.wireOp",EDGE,"E65.top"),sQuery(id+"F2.wireOp",EDGE,"E65.left"),sQuery(id+"F2.wireOp",EDGE,"E65.right")])],"isStart":false}),makeQuery(id+"F5.opExtrude","SWEPT_FACE",FACE,{"disambiguationData":[OSD([sQuery(id+"F4.wireOp",EDGE,"E79.MirrorCS")])]}),makeQuery(id+"F5.opExtrude","SWEPT_FACE",FACE,{"disambiguationData":[OSD([sQuery(id+"F4.wireOp",EDGE,"E95.MirrorCS")])]}),makeQuery(id+"F7.opExtrude","SWEPT_FACE",FACE,{"disambiguationData":[OSD([sQuery(id+"F6.wireOp",EDGE,"E98.right")])]})]});
            cPlane(context, id + "F20", {"entities" : qUnion([Q0]), "cplaneType" : CPlaneType.OFFSET, "offset" : 0 * mm, "width" : 150 * mm, "height" : 150 * mm});
        }
        {
            var Q0;
            Q0=qCreatedBy(id+"F20.planeOp",FACE);
            var sketch = newSketch(context, id + "F21", { "sketchPlane" : qUnion([Q0])});
            skLineSegment(sketch, "E129.bottom", {"start": v(-712.5, -391) * mm, "end": v(-777.5, -391) * mm});
            skLineSegment(sketch, "E129.top", {"start": v(-712.5, -456) * mm, "end": v(-777.5, -456) * mm});
            skLineSegment(sketch, "E129.left", {"start": v(-712.5, -391) * mm, "end": v(-712.5, -456) * mm});
            skLineSegment(sketch, "E129.right", {"start": v(-777.5, -391) * mm, "end": v(-777.5, -456) * mm});
            skSolve(sketch);
        }
        {
            var Q0;
            Q0 = qSketchRegion(id + "F21", true);
            extrude(context, id + "F22", {"entities" : qUnion([Q0]), "operationType" : NewBodyOperationType.ADD, "depth" : 9 * mm, "offsetDistance" : 25 * mm});
        }
        {
            var Q0;
            Q0=makeQuery(id+"F22.opExtrude","CAP_FACE",FACE,{"disambiguationData":[OSD([sQuery(id+"F21.wireOp",EDGE,"E129.bottom"),sQuery(id+"F21.wireOp",EDGE,"E129.top"),sQuery(id+"F21.wireOp",EDGE,"E129.left"),sQuery(id+"F21.wireOp",EDGE,"E129.right")])],"isStart":false});
            var sketch = newSketch(context, id + "F23", { "sketchPlane" : qUnion([Q0])});
            skCircle(sketch, "E130", {"center": v(-764.5, -406) * mm, "radius": 5 * mm});
            skCircle(sketch, "E131", {"center": v(-724.5, -406) * mm, "radius": 5 * mm});
            skCircle(sketch, "E132", {"center": v(-744.5, -436) * mm, "radius": 15 * mm});
            skSolve(sketch);
        }
        {
            var Q0;
            Q0 = qSketchRegion(id + "F23", true);
            extrude(context, id + "F24", {"entities" : qUnion([Q0]), "operationType" : NewBodyOperationType.REMOVE, "oppositeDirection" : true, "depth" : 25 * mm, "offsetDistance" : 25 * mm});
        }
        {
            var Q0;
            Q0=makeQuery(id+"F19.opExtrude","CAP_FACE",FACE,{"disambiguationData":[OSD([sQuery(id+"F18.wireOp",EDGE,"E128.bottom"),sQuery(id+"F18.wireOp",EDGE,"E128.top"),sQuery(id+"F18.wireOp",EDGE,"E128.left"),sQuery(id+"F18.wireOp",EDGE,"E128.right")])],"isStart":false});
            var sketch = newSketch(context, id + "F25", { "sketchPlane" : qUnion([Q0])});
            skCircle(sketch, "E133", {"center": v(725.5, -407) * mm, "radius": 5 * mm});
            skCircle(sketch, "E134", {"center": v(765.5, -407) * mm, "radius": 5 * mm});
            skCircle(sketch, "E135", {"center": v(745.5, -437) * mm, "radius": 15 * mm});
            skSolve(sketch);
        }
        {
            var Q0;
            Q0 = qSketchRegion(id + "F25", true);
            extrude(context, id + "F26", {"entities" : qUnion([Q0]), "operationType" : NewBodyOperationType.REMOVE, "oppositeDirection" : true, "depth" : 25 * mm, "offsetDistance" : 25 * mm});
        }
    });
